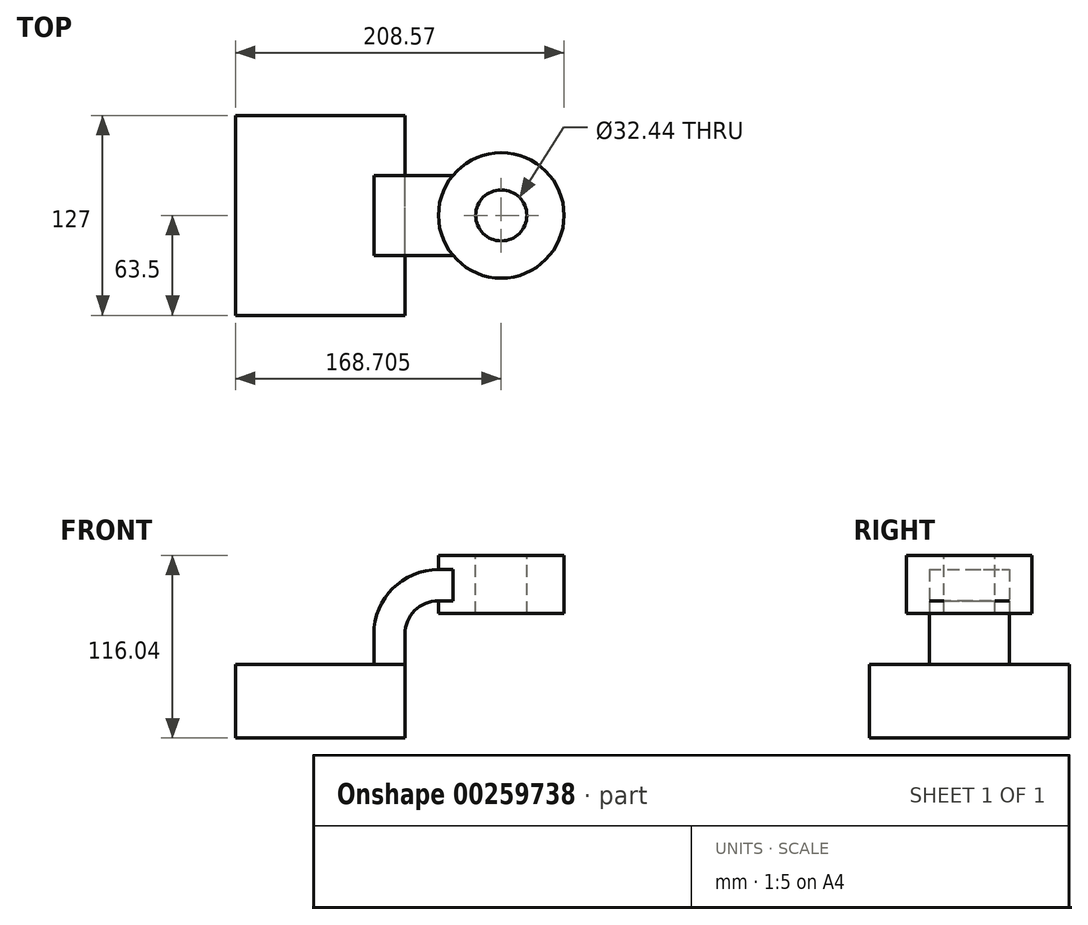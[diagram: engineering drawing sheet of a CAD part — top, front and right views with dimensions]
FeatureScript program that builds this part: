
annotation { "Feature Type Name" : "Feature", "Feature Type Description" : "" }
export const myFeature = defineFeature(function(context is Context, id is Id, definition is map)
    precondition{}
    {
        {
            var Q0;
            Q0=qCreatedBy(makeId("Front.planeOp"),FACE);
            var sketch = newSketch(context, id + "F0", { "sketchPlane" : qUnion([Q0])});
            skLineSegment(sketch, "E0.bottom", {"start": v(53.74, -23.4) * mm, "end": v(-53.74, -23.4) * mm});
            skLineSegment(sketch, "E0.top", {"start": v(53.74, 23.4) * mm, "end": v(-53.74, 23.4) * mm});
            skLineSegment(sketch, "E0.left", {"start": v(53.74, -23.4) * mm, "end": v(53.74, 23.4) * mm});
            skLineSegment(sketch, "E0.right", {"start": v(-53.74, -23.4) * mm, "end": v(-53.74, 23.4) * mm});
            skPoint(sketch, "E0.middle", {"position": v(0, 0) * mm});
            skLineSegment(sketch, "E1.bottom", {"start": v(154.83, 55.95) * mm, "end": v(75.1, 55.95) * mm});
            skLineSegment(sketch, "E1.top", {"start": v(154.83, 92.64) * mm, "end": v(75.1, 92.64) * mm});
            skLineSegment(sketch, "E1.left", {"start": v(154.83, 55.95) * mm, "end": v(154.83, 92.64) * mm});
            skLineSegment(sketch, "E1.right", {"start": v(75.1, 55.95) * mm, "end": v(75.1, 92.64) * mm});
            skPoint(sketch, "E1.middle", {"position": v(114.96, 74.3) * mm});
            skLineSegment(sketch, "E2", {"start": v(53.82, 23.4) * mm, "end": v(53.82, 42.55) * mm});
            skLineSegment(sketch, "E3", {"start": v(75.1, 63.78) * mm, "end": v(75.05, 63.78) * mm});
            skPoint(sketch, "E4.visualSharp", {"position": v(53.82, 63.78) * mm});
            skArc(sketch, "E4.filletArc", {"start": v(75.05, 63.78) * mm, "mid": v(60.04, 57.56) * mm, "end": v(53.82, 42.55) * mm});
            skLineSegment(sketch, "E5.0", {"start": v(34, 23.4) * mm, "end": v(34, 42.55) * mm});
            skArc(sketch, "E5.1", {"start": v(75.05, 83.6) * mm, "mid": v(46.03, 71.57) * mm, "end": v(34, 42.55) * mm});
            skLineSegment(sketch, "E5.2", {"start": v(75.1, 83.6) * mm, "end": v(75.05, 83.6) * mm});
            skLineSegment(sketch, "E6", {"start": v(114.96, 55.95) * mm, "end": v(114.96, 92.64) * mm});
            skLineSegment(sketch, "E7", {"start": v(53.82, 23.4) * mm, "end": v(53.74, 23.4) * mm});
            skLineSegment(sketch, "E8", {"start": v(75.1, 63.78) * mm, "end": v(93.95, 63.7) * mm});
            skLineSegment(sketch, "E9", {"start": v(93.95, 63.7) * mm, "end": v(93.95, 83.6) * mm});
            skLineSegment(sketch, "E10", {"start": v(93.95, 83.6) * mm, "end": v(75.1, 83.6) * mm});
            skSolve(sketch);
        }
        {
            var Q0;
            Q0=makeQuery(id+"F0.imprint","IMPRINT",FACE,{"disambiguationData":[TD([[makeQuery(id+"F0.imprint","IMPRINT",EDGE,{"derivedFrom":sQuery(id+"F0.wireOp",EDGE,"E0.bottom")}),-1.0]])]});
            extrude(context, id + "F1", {"entities" : qUnion([Q0]), "depth" : 127 * mm, "symmetric" : true});
        }
        {
            var Q0;
            Q0=makeQuery(id+"F0.imprint","IMPRINT",FACE,{"disambiguationData":[TD([[makeQuery(id+"F0.imprint","IMPRINT",EDGE,{"derivedFrom":sQuery(id+"F0.wireOp",EDGE,"E2")}),1.0]])]});
            var Q1;
            {var subQ0=sQuery(id+"F0.wireOp",EDGE,"E8");Q1=makeQuery(id+"F0.imprint","IMPRINT",FACE,{"disambiguationData":[TD([[makeQuery(id+"F0.imprint","IMPRINT",EDGE,{"derivedFrom":subQ0}),1.0]])]});}
            extrude(context, id + "F2", {"entities" : qUnion([Q0, Q1]), "offsetDistance" : 25.4 * mm, "depth" : 50.8 * mm, "symmetric" : true});
        }
        {
            var Q0;
            {var subQ0=sQuery(id+"F0.wireOp",EDGE,"E1.left");Q0=makeQuery(id+"F0.imprint","IMPRINT",FACE,{"disambiguationData":[TD([[makeQuery(id+"F0.imprint","IMPRINT",EDGE,{"derivedFrom":subQ0}),1.0]])]});}
            var Q1;
            Q1=sQuery(id+"F0.wireOp",EDGE,"E6");
            revolve(context, id + "F3", {"operationType" : NewBodyOperationType.ADD, "entities" : qUnion([Q0]), "axis" : qUnion([Q1]), "revolveType" : RevolveType.FULL});
        }
        {
            var Q0;
            Q0=makeQuery(id+"F3.opRevolve","SWEPT_FACE",FACE,{"disambiguationData":[OSD([sQuery(id+"F0.wireOp",EDGE,"E1.top")])]});
            var sketch = newSketch(context, id + "F4", { "sketchPlane" : qUnion([Q0])});
            skCircle(sketch, "E11", {"center": v(114.96, 0) * mm, "radius": 16.22 * mm});
            skSolve(sketch);
        }
        {
            var Q0;
            Q0 = qSketchRegion(id + "F4", true);
            extrude(context, id + "F5", {"entities" : qUnion([Q0]), "operationType" : NewBodyOperationType.REMOVE, "endBound" : BoundingType.UP_TO_NEXT, "oppositeDirection" : true, "depth" : 25.4 * mm});
        }
    });
